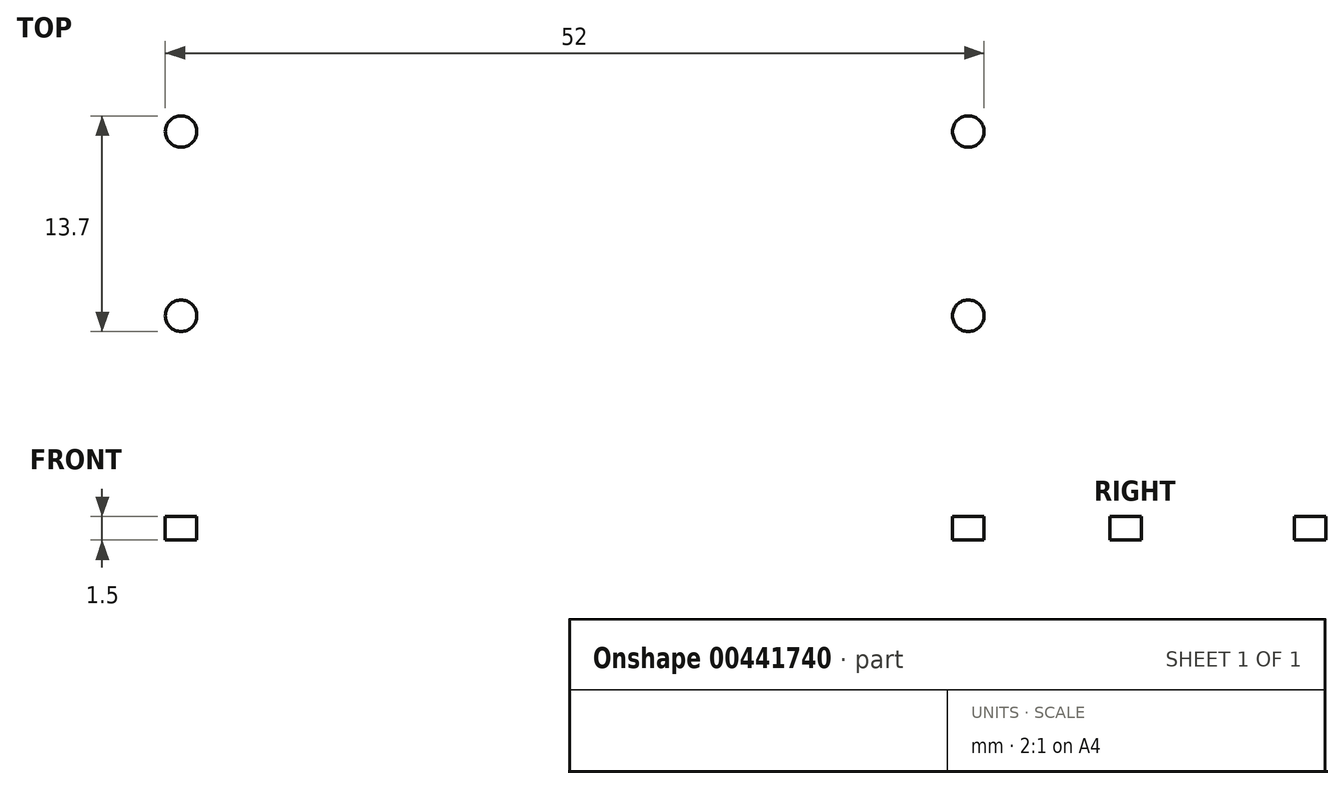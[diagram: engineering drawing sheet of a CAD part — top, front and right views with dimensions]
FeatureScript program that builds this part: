
annotation { "Feature Type Name" : "Feature", "Feature Type Description" : "" }
export const myFeature = defineFeature(function(context is Context, id is Id, definition is map)
    precondition{}
    {
        {
            var Q0;
            Q0=qCreatedBy(makeId("Top.planeOp"),FACE);
            var sketch = newSketch(context, id + "F0", { "sketchPlane" : qUnion([Q0])});
            skLineSegment(sketch, "E0.bottom", {"start": v(50, -10) * mm, "end": v(-50, -10) * mm});
            skLineSegment(sketch, "E0.top", {"start": v(50, 10) * mm, "end": v(-50, 10) * mm});
            skLineSegment(sketch, "E0.left", {"start": v(50, -10) * mm, "end": v(50, 10) * mm});
            skLineSegment(sketch, "E0.right", {"start": v(-50, -10) * mm, "end": v(-50, 10) * mm});
            skPoint(sketch, "E0.middle", {"position": v(0, 0) * mm});
            skSolve(sketch);
        }
        {
            var Q0;
            Q0=makeQuery(id+"F0.imprint","IMPRINT",FACE,{"disambiguationData":[TD([[makeQuery(id+"F0.imprint","IMPRINT",EDGE,{"derivedFrom":sQuery(id+"F0.wireOp",EDGE,"E0.bottom")}),-1.0]])]});
            extrude(context, id + "F1", {"entities" : qUnion([Q0]), "depth" : 1.5 * mm});
        }
        {
            var Q0;
            Q0=makeQuery(id+"F1.opExtrude","CAP_FACE",FACE,{"disambiguationData":[OSD([sQuery(id+"F0.wireOp",EDGE,"E0.bottom"),sQuery(id+"F0.wireOp",EDGE,"E0.top"),sQuery(id+"F0.wireOp",EDGE,"E0.left"),sQuery(id+"F0.wireOp",EDGE,"E0.right")])],"isStart":false});
            var sketch = newSketch(context, id + "F2", { "sketchPlane" : qUnion([Q0])});
            skPoint(sketch, "E1.endSnap0", {"position": v(50, 0) * mm});
            skLineSegment(sketch, "E2", {"start": v(-25, 10) * mm, "end": v(-25, -10) * mm});
            skLineSegment(sketch, "E3", {"start": v(0, 10) * mm, "end": v(0, -10) * mm});
            skLineSegment(sketch, "E4", {"start": v(25, 10) * mm, "end": v(25, -10) * mm});
            skLineSegment(sketch, "E5", {"start": v(-50, 5) * mm, "end": v(50, 5) * mm});
            skLineSegment(sketch, "E6", {"start": v(-50, -5) * mm, "end": v(50, -5) * mm});
            skPoint(sketch, "E7", {"position": v(-25, 0) * mm});
            skPoint(sketch, "E8", {"position": v(0, 0) * mm});
            skPoint(sketch, "E9", {"position": v(25, 0) * mm});
            skPoint(sketch, "E10", {"position": v(-50, 0) * mm});
            skCircle(sketch, "E11", {"center": v(-25, 0) * mm, "radius": 1 * mm});
            skCircle(sketch, "E12", {"center": v(25, 0) * mm, "radius": 1 * mm});
            skSolve(sketch);
        }
        {
            var Q0;
            {var subQ0=sQuery(id+"F2.wireOp",EDGE,"E11");var subQ1=sQuery(id+"F2.wireOp",EDGE,"E2");var subQ2=makeQuery(id+"F2.imprint","INTERSECT",VERTEX,{"disambiguationData":[OD(0.0)],"derivedFrom":[subQ1,subQ0]});Q0=makeQuery(id+"F2.imprint","IMPRINT",FACE,{"disambiguationData":[TD([[makeQuery(id+"F2.imprint","IMPRINT",EDGE,{"disambiguationData":[TD([[subQ2,-1.0]])],"derivedFrom":subQ1}),-1.0]])]});}
            var Q1;
            {var subQ0=sQuery(id+"F2.wireOp",EDGE,"E11");var subQ1=sQuery(id+"F2.wireOp",EDGE,"E2");var subQ2=makeQuery(id+"F2.imprint","INTERSECT",VERTEX,{"disambiguationData":[OD(0.0)],"derivedFrom":[subQ1,subQ0]});Q1=makeQuery(id+"F2.imprint","IMPRINT",FACE,{"disambiguationData":[TD([[makeQuery(id+"F2.imprint","IMPRINT",EDGE,{"disambiguationData":[TD([[subQ2,-1.0]])],"derivedFrom":subQ1}),1.0]])]});}
            var Q2;
            {var subQ0=sQuery(id+"F2.wireOp",EDGE,"E12");var subQ1=sQuery(id+"F2.wireOp",EDGE,"E4");var subQ2=makeQuery(id+"F2.imprint","INTERSECT",VERTEX,{"disambiguationData":[OD(0.0)],"derivedFrom":[subQ1,subQ0]});Q2=makeQuery(id+"F2.imprint","IMPRINT",FACE,{"disambiguationData":[TD([[makeQuery(id+"F2.imprint","IMPRINT",EDGE,{"disambiguationData":[TD([[subQ2,-1.0]])],"derivedFrom":subQ1}),-1.0]])]});}
            var Q3;
            {var subQ0=sQuery(id+"F2.wireOp",EDGE,"E12");var subQ1=sQuery(id+"F2.wireOp",EDGE,"E4");var subQ2=makeQuery(id+"F2.imprint","INTERSECT",VERTEX,{"disambiguationData":[OD(0.0)],"derivedFrom":[subQ1,subQ0]});Q3=makeQuery(id+"F2.imprint","IMPRINT",FACE,{"disambiguationData":[TD([[makeQuery(id+"F2.imprint","IMPRINT",EDGE,{"disambiguationData":[TD([[subQ2,-1.0]])],"derivedFrom":subQ1}),1.0]])]});}
            var Q4;
            {var subQ0=sQuery(id+"F2.wireOp",EDGE,"E2");var subQ1=makeQuery(id+"F1.opExtrude","CAP_EDGE",EDGE,{"disambiguationData":[OSD([sQuery(id+"F0.wireOp",EDGE,"E0.top")])],"isStart":false});var subQ2=makeQuery(id+"F2.imprint","INTERSECT",VERTEX,{"derivedFrom":[subQ1,subQ0]});Q4=makeQuery(id+"F2.imprint","IMPRINT",FACE,{"disambiguationData":[TD([[makeQuery(id+"F2.imprint","IMPRINT",EDGE,{"disambiguationData":[TD([[subQ2,-1.0]])],"derivedFrom":subQ0}),-1.0]])]});}
            var Q5;
            {var subQ0=sQuery(id+"F2.wireOp",EDGE,"E2");var subQ1=makeQuery(id+"F1.opExtrude","CAP_EDGE",EDGE,{"disambiguationData":[OSD([sQuery(id+"F0.wireOp",EDGE,"E0.top")])],"isStart":false});var subQ2=makeQuery(id+"F2.imprint","INTERSECT",VERTEX,{"derivedFrom":[subQ1,subQ0]});Q5=makeQuery(id+"F2.imprint","IMPRINT",FACE,{"disambiguationData":[TD([[makeQuery(id+"F2.imprint","IMPRINT",EDGE,{"disambiguationData":[TD([[subQ2,-1.0]])],"derivedFrom":subQ0}),1.0]])]});}
            var Q6;
            {var subQ0=sQuery(id+"F2.wireOp",EDGE,"E3");var subQ1=makeQuery(id+"F1.opExtrude","CAP_EDGE",EDGE,{"disambiguationData":[OSD([sQuery(id+"F0.wireOp",EDGE,"E0.top")])],"isStart":false});var subQ2=makeQuery(id+"F2.imprint","INTERSECT",VERTEX,{"derivedFrom":[subQ1,subQ0]});Q6=makeQuery(id+"F2.imprint","IMPRINT",FACE,{"disambiguationData":[TD([[makeQuery(id+"F2.imprint","IMPRINT",EDGE,{"disambiguationData":[TD([[subQ2,-1.0]])],"derivedFrom":subQ0}),1.0]])]});}
            var Q7;
            {var subQ0=sQuery(id+"F2.wireOp",EDGE,"E4");var subQ1=makeQuery(id+"F1.opExtrude","CAP_EDGE",EDGE,{"disambiguationData":[OSD([sQuery(id+"F0.wireOp",EDGE,"E0.top")])],"isStart":false});var subQ2=makeQuery(id+"F2.imprint","INTERSECT",VERTEX,{"derivedFrom":[subQ1,subQ0]});Q7=makeQuery(id+"F2.imprint","IMPRINT",FACE,{"disambiguationData":[TD([[makeQuery(id+"F2.imprint","IMPRINT",EDGE,{"disambiguationData":[TD([[subQ2,-1.0]])],"derivedFrom":subQ0}),1.0]])]});}
            var Q8;
            {var subQ0=sQuery(id+"F2.wireOp",EDGE,"E4");var subQ1=makeQuery(id+"F1.opExtrude","CAP_EDGE",EDGE,{"disambiguationData":[OSD([sQuery(id+"F0.wireOp",EDGE,"E0.bottom")])],"isStart":false});var subQ2=makeQuery(id+"F2.imprint","INTERSECT",VERTEX,{"derivedFrom":[subQ1,subQ0]});Q8=makeQuery(id+"F2.imprint","IMPRINT",FACE,{"disambiguationData":[TD([[makeQuery(id+"F2.imprint","IMPRINT",EDGE,{"disambiguationData":[TD([[subQ2,1.0]])],"derivedFrom":subQ0}),1.0]])]});}
            var Q9;
            {var subQ0=sQuery(id+"F2.wireOp",EDGE,"E3");var subQ1=makeQuery(id+"F1.opExtrude","CAP_EDGE",EDGE,{"disambiguationData":[OSD([sQuery(id+"F0.wireOp",EDGE,"E0.bottom")])],"isStart":false});var subQ2=makeQuery(id+"F2.imprint","INTERSECT",VERTEX,{"derivedFrom":[subQ1,subQ0]});Q9=makeQuery(id+"F2.imprint","IMPRINT",FACE,{"disambiguationData":[TD([[makeQuery(id+"F2.imprint","IMPRINT",EDGE,{"disambiguationData":[TD([[subQ2,1.0]])],"derivedFrom":subQ0}),1.0]])]});}
            var Q10;
            {var subQ0=sQuery(id+"F2.wireOp",EDGE,"E2");var subQ1=makeQuery(id+"F1.opExtrude","CAP_EDGE",EDGE,{"disambiguationData":[OSD([sQuery(id+"F0.wireOp",EDGE,"E0.bottom")])],"isStart":false});var subQ2=makeQuery(id+"F2.imprint","INTERSECT",VERTEX,{"derivedFrom":[subQ1,subQ0]});Q10=makeQuery(id+"F2.imprint","IMPRINT",FACE,{"disambiguationData":[TD([[makeQuery(id+"F2.imprint","IMPRINT",EDGE,{"disambiguationData":[TD([[subQ2,1.0]])],"derivedFrom":subQ0}),1.0]])]});}
            var Q11;
            {var subQ0=sQuery(id+"F2.wireOp",EDGE,"E2");var subQ1=makeQuery(id+"F1.opExtrude","CAP_EDGE",EDGE,{"disambiguationData":[OSD([sQuery(id+"F0.wireOp",EDGE,"E0.bottom")])],"isStart":false});var subQ2=makeQuery(id+"F2.imprint","INTERSECT",VERTEX,{"derivedFrom":[subQ1,subQ0]});Q11=makeQuery(id+"F2.imprint","IMPRINT",FACE,{"disambiguationData":[TD([[makeQuery(id+"F2.imprint","IMPRINT",EDGE,{"disambiguationData":[TD([[subQ2,1.0]])],"derivedFrom":subQ0}),-1.0]])]});}
            extrude(context, id + "F3", {"entities" : qUnion([Q0, Q1, Q2, Q3, Q4, Q5, Q6, Q7, Q8, Q9, Q10, Q11]), "operationType" : NewBodyOperationType.REMOVE, "endBound" : BoundingType.THROUGH_ALL, "oppositeDirection" : true, "depth" : 25 * mm});
        }
        {
            var Q0;
            Q0=makeQuery(id+"F1.opExtrude","CAP_FACE",FACE,{"disambiguationData":[OSD([sQuery(id+"F0.wireOp",EDGE,"E0.bottom"),sQuery(id+"F0.wireOp",EDGE,"E0.top"),sQuery(id+"F0.wireOp",EDGE,"E0.left"),sQuery(id+"F0.wireOp",EDGE,"E0.right")])],"isStart":false});
            var sketch = newSketch(context, id + "F4", { "sketchPlane" : qUnion([Q0])});
            skLineSegment(sketch, "E13", {"start": v(-50, 0) * mm, "end": v(-40, 0) * mm});
            skLineSegment(sketch, "E14", {"start": v(-40, 0) * mm, "end": v(-30, 0) * mm});
            skLineSegment(sketch, "E15", {"start": v(-30, 0) * mm, "end": v(-20, 0) * mm});
            skLineSegment(sketch, "E16", {"start": v(-20, 0) * mm, "end": v(-10, 0) * mm});
            skLineSegment(sketch, "E17", {"start": v(-10, 0) * mm, "end": v(0, 0) * mm});
            skLineSegment(sketch, "E18", {"start": v(0, 0) * mm, "end": v(10, 0) * mm});
            skLineSegment(sketch, "E19", {"start": v(10, 0) * mm, "end": v(20, 0) * mm});
            skLineSegment(sketch, "E20", {"start": v(20, 0) * mm, "end": v(30, 0) * mm});
            skLineSegment(sketch, "E21", {"start": v(30, 0) * mm, "end": v(40, 0) * mm});
            skLineSegment(sketch, "E22", {"start": v(40, 0) * mm, "end": v(50, 0) * mm});
            skPoint(sketch, "E23", {"position": v(-40, 5) * mm});
            skPoint(sketch, "E24", {"position": v(-40, -5) * mm});
            skPoint(sketch, "E25", {"position": v(-30, 5) * mm});
            skPoint(sketch, "E26", {"position": v(-30, -5) * mm});
            skPoint(sketch, "E27", {"position": v(40, 5) * mm});
            skPoint(sketch, "E28", {"position": v(40, -5) * mm});
            skPoint(sketch, "E29", {"position": v(30, 5) * mm});
            skPoint(sketch, "E30", {"position": v(30, -5) * mm});
            skCircle(sketch, "E31", {"center": v(-40, 5) * mm, "radius": 1.5 * mm});
            skCircle(sketch, "E32", {"center": v(-40, -5) * mm, "radius": 1.5 * mm});
            skCircle(sketch, "E33", {"center": v(-30, -5) * mm, "radius": 1.5 * mm});
            skCircle(sketch, "E34", {"center": v(-30, 5) * mm, "radius": 1.5 * mm});
            skCircle(sketch, "E35", {"center": v(30, 5) * mm, "radius": 1.5 * mm});
            skCircle(sketch, "E36", {"center": v(30, -5) * mm, "radius": 1.5 * mm});
            skCircle(sketch, "E37", {"center": v(40, 5) * mm, "radius": 1.5 * mm});
            skCircle(sketch, "E38", {"center": v(40, -5) * mm, "radius": 1.5 * mm});
            skSolve(sketch);
        }
        {
            var Q0;
            {var subQ0=sQuery(id+"F4.wireOp",EDGE,"E31");var subQ1=makeQuery(id+"F3.boolean.opBoolean","COPY",EDGE,{"derivedFrom":makeQuery(id+"F3.opExtrude","CAP_EDGE",EDGE,{"disambiguationData":[OSD([sQuery(id+"F2.wireOp",EDGE,"E5")])],"isStart":true})});var subQ2=makeQuery(id+"F4.imprint","INTERSECT",VERTEX,{"disambiguationData":[OD(0.0)],"derivedFrom":[subQ1,subQ0]});Q0=makeQuery(id+"F4.imprint","IMPRINT",FACE,{"disambiguationData":[TD([[makeQuery(id+"F4.imprint","IMPRINT",EDGE,{"disambiguationData":[TD([[subQ2,-1.0]])],"derivedFrom":subQ0}),1.0]])]});}
            var Q1;
            {var subQ0=sQuery(id+"F4.wireOp",EDGE,"E34");var subQ1=makeQuery(id+"F3.boolean.opBoolean","COPY",EDGE,{"derivedFrom":makeQuery(id+"F3.opExtrude","CAP_EDGE",EDGE,{"disambiguationData":[OSD([sQuery(id+"F2.wireOp",EDGE,"E5")])],"isStart":true})});var subQ2=makeQuery(id+"F4.imprint","INTERSECT",VERTEX,{"disambiguationData":[OD(0.0)],"derivedFrom":[subQ1,subQ0]});Q1=makeQuery(id+"F4.imprint","IMPRINT",FACE,{"disambiguationData":[TD([[makeQuery(id+"F4.imprint","IMPRINT",EDGE,{"disambiguationData":[TD([[subQ2,-1.0]])],"derivedFrom":subQ0}),1.0]])]});}
            var Q2;
            {var subQ0=sQuery(id+"F4.wireOp",EDGE,"E32");var subQ1=makeQuery(id+"F3.boolean.opBoolean","COPY",EDGE,{"derivedFrom":makeQuery(id+"F3.opExtrude","CAP_EDGE",EDGE,{"disambiguationData":[OSD([sQuery(id+"F2.wireOp",EDGE,"E6")])],"isStart":true})});var subQ2=makeQuery(id+"F4.imprint","INTERSECT",VERTEX,{"disambiguationData":[OD(0.0)],"derivedFrom":[subQ1,subQ0]});Q2=makeQuery(id+"F4.imprint","IMPRINT",FACE,{"disambiguationData":[TD([[makeQuery(id+"F4.imprint","IMPRINT",EDGE,{"disambiguationData":[TD([[subQ2,1.0]])],"derivedFrom":subQ0}),1.0]])]});}
            var Q3;
            {var subQ0=sQuery(id+"F4.wireOp",EDGE,"E33");var subQ1=makeQuery(id+"F3.boolean.opBoolean","COPY",EDGE,{"derivedFrom":makeQuery(id+"F3.opExtrude","CAP_EDGE",EDGE,{"disambiguationData":[OSD([sQuery(id+"F2.wireOp",EDGE,"E6")])],"isStart":true})});var subQ2=makeQuery(id+"F4.imprint","INTERSECT",VERTEX,{"disambiguationData":[OD(0.0)],"derivedFrom":[subQ1,subQ0]});Q3=makeQuery(id+"F4.imprint","IMPRINT",FACE,{"disambiguationData":[TD([[makeQuery(id+"F4.imprint","IMPRINT",EDGE,{"disambiguationData":[TD([[subQ2,1.0]])],"derivedFrom":subQ0}),1.0]])]});}
            var Q4;
            {var subQ0=sQuery(id+"F4.wireOp",EDGE,"E35");var subQ1=makeQuery(id+"F3.boolean.opBoolean","COPY",EDGE,{"derivedFrom":makeQuery(id+"F3.opExtrude","CAP_EDGE",EDGE,{"disambiguationData":[OSD([sQuery(id+"F2.wireOp",EDGE,"E5")])],"isStart":true})});var subQ2=makeQuery(id+"F4.imprint","INTERSECT",VERTEX,{"disambiguationData":[OD(0.0)],"derivedFrom":[subQ1,subQ0]});Q4=makeQuery(id+"F4.imprint","IMPRINT",FACE,{"disambiguationData":[TD([[makeQuery(id+"F4.imprint","IMPRINT",EDGE,{"disambiguationData":[TD([[subQ2,1.0]])],"derivedFrom":subQ0}),1.0]])]});}
            var Q5;
            {var subQ0=sQuery(id+"F4.wireOp",EDGE,"E36");var subQ1=makeQuery(id+"F3.boolean.opBoolean","COPY",EDGE,{"derivedFrom":makeQuery(id+"F3.opExtrude","CAP_EDGE",EDGE,{"disambiguationData":[OSD([sQuery(id+"F2.wireOp",EDGE,"E6")])],"isStart":true})});var subQ2=makeQuery(id+"F4.imprint","INTERSECT",VERTEX,{"disambiguationData":[OD(0.0)],"derivedFrom":[subQ1,subQ0]});Q5=makeQuery(id+"F4.imprint","IMPRINT",FACE,{"disambiguationData":[TD([[makeQuery(id+"F4.imprint","IMPRINT",EDGE,{"disambiguationData":[TD([[subQ2,-1.0]])],"derivedFrom":subQ0}),1.0]])]});}
            var Q6;
            {var subQ0=sQuery(id+"F4.wireOp",EDGE,"E38");var subQ1=makeQuery(id+"F3.boolean.opBoolean","COPY",EDGE,{"derivedFrom":makeQuery(id+"F3.opExtrude","CAP_EDGE",EDGE,{"disambiguationData":[OSD([sQuery(id+"F2.wireOp",EDGE,"E6")])],"isStart":true})});var subQ2=makeQuery(id+"F4.imprint","INTERSECT",VERTEX,{"disambiguationData":[OD(0.0)],"derivedFrom":[subQ1,subQ0]});Q6=makeQuery(id+"F4.imprint","IMPRINT",FACE,{"disambiguationData":[TD([[makeQuery(id+"F4.imprint","IMPRINT",EDGE,{"disambiguationData":[TD([[subQ2,-1.0]])],"derivedFrom":subQ0}),1.0]])]});}
            var Q7;
            {var subQ0=sQuery(id+"F4.wireOp",EDGE,"E37");var subQ1=makeQuery(id+"F3.boolean.opBoolean","COPY",EDGE,{"derivedFrom":makeQuery(id+"F3.opExtrude","CAP_EDGE",EDGE,{"disambiguationData":[OSD([sQuery(id+"F2.wireOp",EDGE,"E5")])],"isStart":true})});var subQ2=makeQuery(id+"F4.imprint","INTERSECT",VERTEX,{"disambiguationData":[OD(0.0)],"derivedFrom":[subQ1,subQ0]});Q7=makeQuery(id+"F4.imprint","IMPRINT",FACE,{"disambiguationData":[TD([[makeQuery(id+"F4.imprint","IMPRINT",EDGE,{"disambiguationData":[TD([[subQ2,1.0]])],"derivedFrom":subQ0}),1.0]])]});}
            extrude(context, id + "F5", {"entities" : qUnion([Q0, Q1, Q2, Q3, Q4, Q5, Q6, Q7]), "operationType" : NewBodyOperationType.REMOVE, "endBound" : BoundingType.THROUGH_ALL, "oppositeDirection" : true, "depth" : 25 * mm});
        }
        {
            var Q0;
            Q0=makeQuery(id+"F1.opExtrude","CAP_FACE",FACE,{"disambiguationData":[OSD([sQuery(id+"F0.wireOp",EDGE,"E0.bottom"),sQuery(id+"F0.wireOp",EDGE,"E0.top"),sQuery(id+"F0.wireOp",EDGE,"E0.left"),sQuery(id+"F0.wireOp",EDGE,"E0.right")])],"isStart":false});
            var sketch = newSketch(context, id + "F6", { "sketchPlane" : qUnion([Q0])});
            skLineSegment(sketch, "E39", {"start": v(0, 5) * mm, "end": v(0, 2.5) * mm});
            skLineSegment(sketch, "E40", {"start": v(0, 2.5) * mm, "end": v(0, 0) * mm});
            skLineSegment(sketch, "E41", {"start": v(0, 0) * mm, "end": v(0, -2.5) * mm});
            skLineSegment(sketch, "E42", {"start": v(0, -2.5) * mm, "end": v(0, -5) * mm});
            skCircle(sketch, "E43", {"center": v(0, 2.5) * mm, "radius": 1.25 * mm});
            skCircle(sketch, "E44", {"center": v(0, -2.5) * mm, "radius": 1.25 * mm});
            skSolve(sketch);
        }
        {
            var Q0;
            {var subQ0=sQuery(id+"F6.wireOp",EDGE,"E40");var subQ1=sQuery(id+"F6.wireOp",EDGE,"E39");var subQ2=makeQuery(id+"F6.imprint","INTERSECT",VERTEX,{"derivedFrom":[subQ1,subQ0]});Q0=makeQuery(id+"F6.imprint","IMPRINT",FACE,{"disambiguationData":[TD([[makeQuery(id+"F6.imprint","IMPRINT",EDGE,{"disambiguationData":[TD([[subQ2,1.0]])],"derivedFrom":subQ1}),-1.0]])]});}
            var Q1;
            {var subQ0=sQuery(id+"F6.wireOp",EDGE,"E40");var subQ1=sQuery(id+"F6.wireOp",EDGE,"E39");var subQ2=makeQuery(id+"F6.imprint","INTERSECT",VERTEX,{"derivedFrom":[subQ1,subQ0]});Q1=makeQuery(id+"F6.imprint","IMPRINT",FACE,{"disambiguationData":[TD([[makeQuery(id+"F6.imprint","IMPRINT",EDGE,{"disambiguationData":[TD([[subQ2,1.0]])],"derivedFrom":subQ1}),1.0]])]});}
            var Q2;
            {var subQ0=sQuery(id+"F6.wireOp",EDGE,"E42");var subQ1=sQuery(id+"F6.wireOp",EDGE,"E41");var subQ2=makeQuery(id+"F6.imprint","INTERSECT",VERTEX,{"derivedFrom":[subQ1,subQ0]});Q2=makeQuery(id+"F6.imprint","IMPRINT",FACE,{"disambiguationData":[TD([[makeQuery(id+"F6.imprint","IMPRINT",EDGE,{"disambiguationData":[TD([[subQ2,1.0]])],"derivedFrom":subQ1}),1.0]])]});}
            var Q3;
            {var subQ0=sQuery(id+"F6.wireOp",EDGE,"E42");var subQ1=sQuery(id+"F6.wireOp",EDGE,"E41");var subQ2=makeQuery(id+"F6.imprint","INTERSECT",VERTEX,{"derivedFrom":[subQ1,subQ0]});Q3=makeQuery(id+"F6.imprint","IMPRINT",FACE,{"disambiguationData":[TD([[makeQuery(id+"F6.imprint","IMPRINT",EDGE,{"disambiguationData":[TD([[subQ2,1.0]])],"derivedFrom":subQ1}),-1.0]])]});}
            extrude(context, id + "F7", {"entities" : qUnion([Q0, Q1, Q2, Q3]), "operationType" : NewBodyOperationType.REMOVE, "endBound" : BoundingType.THROUGH_ALL, "oppositeDirection" : true, "depth" : 25 * mm});
        }
        {
            var Q0;
            Q0=makeQuery(id+"F1.opExtrude","SWEPT_BODY",BODY,{"disambiguationData":[OSD([sQuery(id+"F0.wireOp",EDGE,"E0.bottom"),sQuery(id+"F0.wireOp",EDGE,"E0.top"),sQuery(id+"F0.wireOp",EDGE,"E0.left"),sQuery(id+"F0.wireOp",EDGE,"E0.right")])]});
            transform(context, id + "F8", {"entities" : qUnion([Q0]), "transformType" : TransformType.TRANSLATION_3D, "dx" : 0 * mm, "dy" : -11.7 * mm, "dz" : 0 * mm, "makeCopy" : true});
        }
    });
